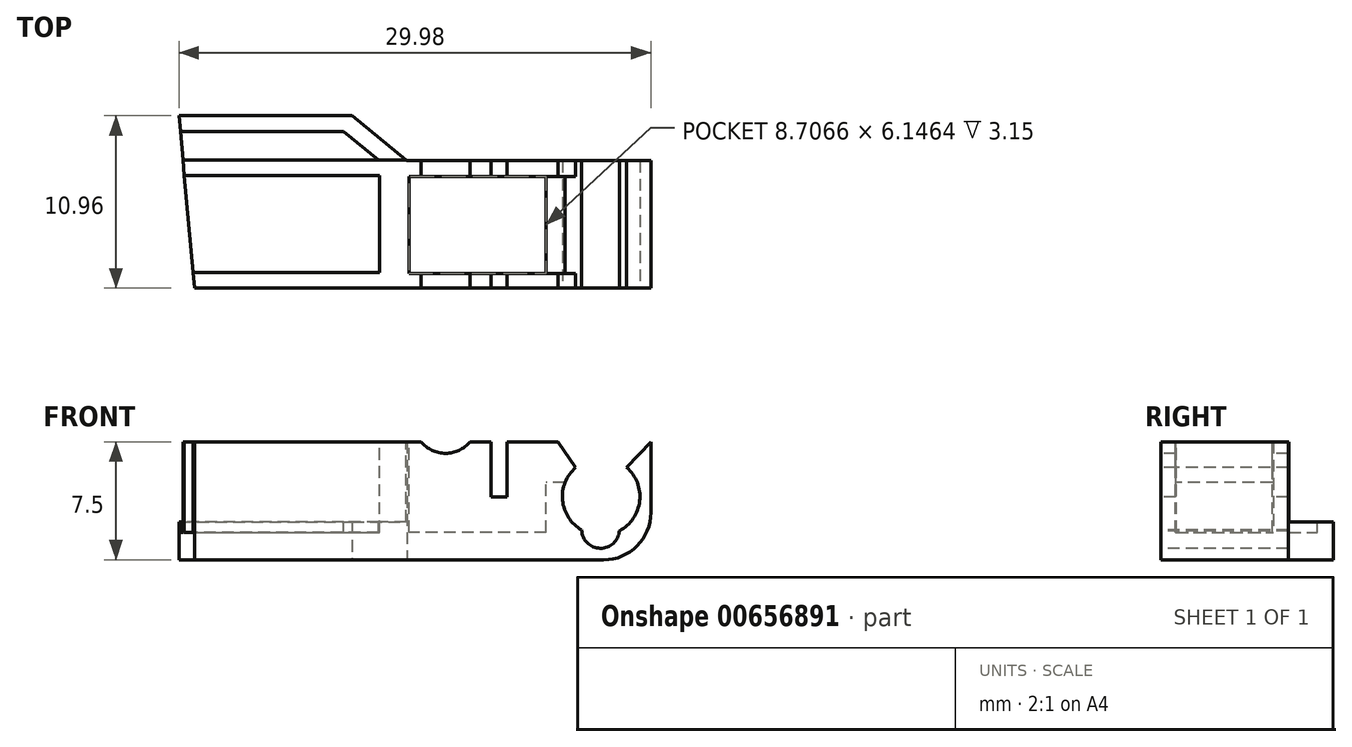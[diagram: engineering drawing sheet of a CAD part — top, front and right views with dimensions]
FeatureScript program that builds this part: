
annotation { "Feature Type Name" : "Feature", "Feature Type Description" : "" }
export const myFeature = defineFeature(function(context is Context, id is Id, definition is map)
    precondition{}
    {
        {
            var Q0;
            Q0=qCreatedBy(makeId("Top.planeOp"),FACE);
            var sketch = newSketch(context, id + "F0", { "sketchPlane" : qUnion([Q0])});
            skLineSegment(sketch, "E0", {"start": v(-51.52, -15.58) * mm, "end": v(-52.5, -4.62) * mm});
            skLineSegment(sketch, "E1", {"start": v(-52.5, -4.62) * mm, "end": v(-41.5, -4.62) * mm});
            skLineSegment(sketch, "E2", {"start": v(-41.5, -4.62) * mm, "end": v(-38.02, -7.48) * mm});
            skLineSegment(sketch, "E3", {"start": v(-38.02, -7.48) * mm, "end": v(-22.52, -7.48) * mm});
            skLineSegment(sketch, "E4", {"start": v(-22.52, -7.48) * mm, "end": v(-22.52, -15.58) * mm});
            skLineSegment(sketch, "E5", {"start": v(-22.52, -15.58) * mm, "end": v(-51.52, -15.58) * mm});
            skSolve(sketch);
        }
        {
            var Q0;
            Q0 = qSketchRegion(id + "F0", true);
            extrude(context, id + "F1", {"entities" : qUnion([Q0]), "depth" : 7.5 * mm, "offsetDistance" : 25 * mm});
        }
        {
            var Q0;
            Q0=makeQuery(id+"F1.opExtrude","CAP_FACE",FACE,{"disambiguationData":[OSD([sQuery(id+"F0.wireOp",EDGE,"E0"),sQuery(id+"F0.wireOp",EDGE,"E1"),sQuery(id+"F0.wireOp",EDGE,"E2"),sQuery(id+"F0.wireOp",EDGE,"E3"),sQuery(id+"F0.wireOp",EDGE,"E4"),sQuery(id+"F0.wireOp",EDGE,"E5")])],"isStart":false});
            var sketch = newSketch(context, id + "F2", { "sketchPlane" : qUnion([Q0])});
            skLineSegment(sketch, "E6", {"start": v(-54.3, -14.58) * mm, "end": v(-39.74, -14.58) * mm});
            skLineSegment(sketch, "E7", {"start": v(-39.74, -14.58) * mm, "end": v(-39.74, -8.43) * mm});
            skLineSegment(sketch, "E8", {"start": v(-39.74, -8.43) * mm, "end": v(-53.75, -8.43) * mm});
            skLineSegment(sketch, "E9", {"start": v(-52.4, -5.62) * mm, "end": v(-42.03, -5.62) * mm});
            skLineSegment(sketch, "E10", {"start": v(-42.03, -5.62) * mm, "end": v(-39.81, -7.44) * mm});
            skLineSegment(sketch, "E11", {"start": v(-39.81, -7.44) * mm, "end": v(-52.24, -7.44) * mm});
            skLineSegment(sketch, "E12", {"start": v(-29.17, -8.5) * mm, "end": v(-37.88, -8.5) * mm});
            skLineSegment(sketch, "E13", {"start": v(-37.88, -8.5) * mm, "end": v(-37.88, -14.64) * mm});
            skLineSegment(sketch, "E14", {"start": v(-37.88, -14.64) * mm, "end": v(-29.17, -14.64) * mm});
            skLineSegment(sketch, "E15", {"start": v(-29.17, -14.64) * mm, "end": v(-29.17, -8.5) * mm});
            skLineSegment(sketch, "E16", {"start": v(-53.75, -8.43) * mm, "end": v(-54.3, -14.58) * mm});
            skLineSegment(sketch, "E17", {"start": v(-52.4, -5.62) * mm, "end": v(-52.24, -7.44) * mm});
            skSolve(sketch);
        }
        {
            var Q0;
            Q0 = qSketchRegion(id + "F2", true);
            extrude(context, id + "F3", {"entities" : qUnion([Q0]), "operationType" : NewBodyOperationType.REMOVE, "oppositeDirection" : true, "depth" : 5.75 * mm, "offsetDistance" : 25 * mm});
        }
        {
            var Q0;
            Q0=makeQuery(id+"F1.opExtrude","SWEPT_FACE",FACE,{"disambiguationData":[OSD([sQuery(id+"F0.wireOp",EDGE,"E5")])]});
            var sketch = newSketch(context, id + "F4", { "sketchPlane" : qUnion([Q0])});
            skCircle(sketch, "E18", {"center": v(-35.56, 8.76) * mm, "radius": 2 * mm});
            skSolve(sketch);
        }
        {
            var Q0;
            {var subQ0=sQuery(id+"F4.wireOp",EDGE,"E18");var subQ1=makeQuery(id+"F1.opExtrude","CAP_EDGE",EDGE,{"disambiguationData":[OSD([sQuery(id+"F0.wireOp",EDGE,"E5")])],"isStart":false});var subQ2=makeQuery(id+"F4.imprint","INTERSECT",VERTEX,{"disambiguationData":[OD(0.0)],"derivedFrom":[subQ1,subQ0]});Q0=makeQuery(id+"F4.imprint","IMPRINT",FACE,{"disambiguationData":[TD([[makeQuery(id+"F4.imprint","IMPRINT",EDGE,{"disambiguationData":[TD([[subQ2,-1.0]])],"derivedFrom":subQ0}),1.0]])]});}
            var Q1;
            Q1=sQuery(id+"F4.wireOp",EDGE,"E18");
            extrude(context, id + "F5", {"entities" : qUnion([Q0]), "operationType" : NewBodyOperationType.REMOVE, "surfaceEntities" : qUnion([Q1]), "oppositeDirection" : true, "depth" : 25 * mm, "offsetDistance" : 25 * mm});
        }
        {
            var Q0;
            Q0=makeQuery(id+"F1.opExtrude","SWEPT_FACE",FACE,{"disambiguationData":[OSD([sQuery(id+"F0.wireOp",EDGE,"E5")])]});
            var sketch = newSketch(context, id + "F6", { "sketchPlane" : qUnion([Q0])});
            skLineSegment(sketch, "E19.bottom", {"start": v(-31.67, 7.5) * mm, "end": v(-32.67, 7.5) * mm});
            skLineSegment(sketch, "E19.top", {"start": v(-31.67, 4) * mm, "end": v(-32.67, 4) * mm});
            skLineSegment(sketch, "E19.left", {"start": v(-31.67, 7.5) * mm, "end": v(-31.67, 4) * mm});
            skLineSegment(sketch, "E19.right", {"start": v(-32.67, 7.5) * mm, "end": v(-32.67, 4) * mm});
            skSolve(sketch);
        }
        {
            var Q0;
            Q0=makeQuery(id+"F6.imprint","IMPRINT",FACE,{"disambiguationData":[TD([[makeQuery(id+"F6.imprint","IMPRINT",EDGE,{"derivedFrom":sQuery(id+"F6.wireOp",EDGE,"E19.bottom")}),1.0]])]});
            extrude(context, id + "F7", {"entities" : qUnion([Q0]), "operationType" : NewBodyOperationType.REMOVE, "oppositeDirection" : true, "depth" : 25 * mm, "offsetDistance" : 25 * mm});
        }
        {
            var Q0;
            Q0=makeQuery(id+"F1.opExtrude","SWEPT_FACE",FACE,{"disambiguationData":[OSD([sQuery(id+"F0.wireOp",EDGE,"E5")])]});
            var sketch = newSketch(context, id + "F8", { "sketchPlane" : qUnion([Q0])});
            skCircle(sketch, "E20", {"center": v(-25.68, 4.01) * mm, "radius": 2.46 * mm});
            skCircle(sketch, "E21", {"center": v(-25.72, 1.93) * mm, "radius": 1.2 * mm});
            skLineSegment(sketch, "E22", {"start": v(-28.4, 7.5) * mm, "end": v(-22.52, 7.5) * mm});
            skLineSegment(sketch, "E23", {"start": v(-28.4, 7.5) * mm, "end": v(-27.3, 5.87) * mm});
            skLineSegment(sketch, "E24", {"start": v(-27.3, 5.87) * mm, "end": v(-24.06, 5.87) * mm});
            skLineSegment(sketch, "E25", {"start": v(-24.06, 5.87) * mm, "end": v(-22.52, 7.5) * mm});
            skSolve(sketch);
        }
        {
            var Q0;
            Q0 = qSketchRegion(id + "F8", true);
            extrude(context, id + "F9", {"entities" : qUnion([Q0]), "operationType" : NewBodyOperationType.REMOVE, "oppositeDirection" : true, "depth" : 25 * mm, "offsetDistance" : 25 * mm});
        }
        {
            var Q0;
            Q0=makeQuery(id+"F1.opExtrude","CAP_EDGE",EDGE,{"disambiguationData":[OSD([sQuery(id+"F0.wireOp",EDGE,"E4")])],"isStart":true});
            fillet(context, id + "F10", {"entities" : qUnion([Q0]), "radius" : 3 * mm, "tangentPropagation" : true, "allowEdgeOverflow" : false});
        }
        {
            var Q0;
            Q0=makeQuery(id+"F3.boolean.opBoolean","COPY",FACE,{"derivedFrom":makeQuery(id+"F3.opExtrude","SWEPT_FACE",FACE,{"disambiguationData":[OSD([sQuery(id+"F2.wireOp",EDGE,"E15")])]})});
            var sketch = newSketch(context, id + "F11", { "sketchPlane" : qUnion([Q0])});
            skLineSegment(sketch, "E26.bottom", {"start": v(8.5, 7.5) * mm, "end": v(14.64, 7.5) * mm});
            skLineSegment(sketch, "E26.top", {"start": v(8.5, 4.9) * mm, "end": v(14.64, 4.9) * mm});
            skLineSegment(sketch, "E26.left", {"start": v(8.5, 7.5) * mm, "end": v(8.5, 4.9) * mm});
            skLineSegment(sketch, "E26.right", {"start": v(14.64, 7.5) * mm, "end": v(14.64, 4.9) * mm});
            skSolve(sketch);
        }
        {
            var Q0;
            Q0 = qSketchRegion(id + "F11", true);
            extrude(context, id + "F12", {"entities" : qUnion([Q0]), "operationType" : NewBodyOperationType.REMOVE, "oppositeDirection" : true, "depth" : 2 * mm, "offsetDistance" : 25 * mm});
        }
        {
            var Q0;
            Q0=makeQuery(id+"F3.boolean.opBoolean","COPY",FACE,{"derivedFrom":makeQuery(id+"F3.opExtrude","SWEPT_FACE",FACE,{"disambiguationData":[OSD([sQuery(id+"F2.wireOp",EDGE,"E11")])]})});
            var sketch = newSketch(context, id + "F13", { "sketchPlane" : qUnion([Q0])});
            skLineSegment(sketch, "E27.bottom", {"start": v(39.81, 7.5) * mm, "end": v(52.24, 7.5) * mm});
            skLineSegment(sketch, "E27.top", {"start": v(39.81, 2.23) * mm, "end": v(52.24, 2.23) * mm});
            skLineSegment(sketch, "E27.left", {"start": v(39.81, 7.5) * mm, "end": v(39.81, 2.23) * mm});
            skLineSegment(sketch, "E27.right", {"start": v(52.24, 7.5) * mm, "end": v(52.24, 2.23) * mm});
            skSolve(sketch);
        }
        {
            var Q0;
            Q0=makeQuery(id+"F13.imprint","IMPRINT",FACE,{"disambiguationData":[TD([[makeQuery(id+"F13.imprint","IMPRINT",EDGE,{"derivedFrom":sQuery(id+"F13.wireOp",EDGE,"E27.bottom")}),-1.0]])]});
            var sketch = newSketch(context, id + "F14", { "sketchPlane" : qUnion([Q0])});
            skLineSegment(sketch, "E28.bottom", {"start": v(37.95, 7.5) * mm, "end": v(57.48, 7.5) * mm});
            skLineSegment(sketch, "E28.top", {"start": v(37.95, 2.41) * mm, "end": v(57.48, 2.41) * mm});
            skLineSegment(sketch, "E28.left", {"start": v(37.95, 7.5) * mm, "end": v(37.95, 2.41) * mm});
            skLineSegment(sketch, "E28.right", {"start": v(57.48, 7.5) * mm, "end": v(57.48, 2.41) * mm});
            skSolve(sketch);
        }
        {
            var Q0;
            Q0 = qSketchRegion(id + "F14", true);
            extrude(context, id + "F15", {"entities" : qUnion([Q0]), "operationType" : NewBodyOperationType.REMOVE, "depth" : 25 * mm, "offsetDistance" : 25 * mm});
        }
    });
